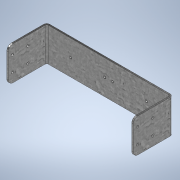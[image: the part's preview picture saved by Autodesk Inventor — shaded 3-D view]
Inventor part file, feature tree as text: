
AUTODESK INVENTOR PART (.ipt)
format: ipt  version: 2022 (Build 260153000, 153)  size: 213,504 bytes
history: native  units: mm
features: sheet_metal_op x4, sketch x4, other x3, hole x2, chamfer x1
ambient origin geometry x8: Origin, YZ Plane, XZ Plane, XY Plane, X Axis, Y Axis, Z Axis, Center Point
bodies: Solid1 (feature_tree)
feature tree (14):
  sheet_metal_op  "Face1"
  sheet_metal_op  "Flange1"
  hole  "Hole1"  [1 undecoded]
  chamfer  "Corner Round1"
  hole  "Hole2"  [1 undecoded]
  sketch  "Sketch1"  dims[d0=161.0mm d1=44.0mm]
  other  "Plate1"
  sketch  "Sketch2"  dims[d2=2.0mm d3=2.0mm]
  other  "Plate2"
  sheet_metal_op  "Bend1"
  sheet_metal_op  "Corner1"
  sketch  "Sketch3"  dims[d4=1.0mm]
  sketch  "Sketch4"  dims[d5=4.0mm d6=2.0mm d7=52.0mm d8=90.0deg d9=2.0mm d10=8.0mm d11=2.0mm d12=2.0mm d13=20.0mm d14=20.0mm d15=5.5mm d16=3.4mm d17=6.0mm d18=6.3mm d19=2.0mm d20=90.0deg d21=2.0mm d22=20.594885mm d23=6.0mm d24=10.0mm d25=33.0mm d26=33.0mm d27=44.5mm d28=44.5mm d29=3.4mm d30=6.0mm d31=4.0mm d32=2.0mm d33=90.0deg d34=8.0mm d35=20.594885mm]
  other  "Definition1"
note: 2 required parameter values undecoded (feature->parameter linkage not recoverable at this tier; creation-order binding heuristic only, values carry confidence <= 0.55)
